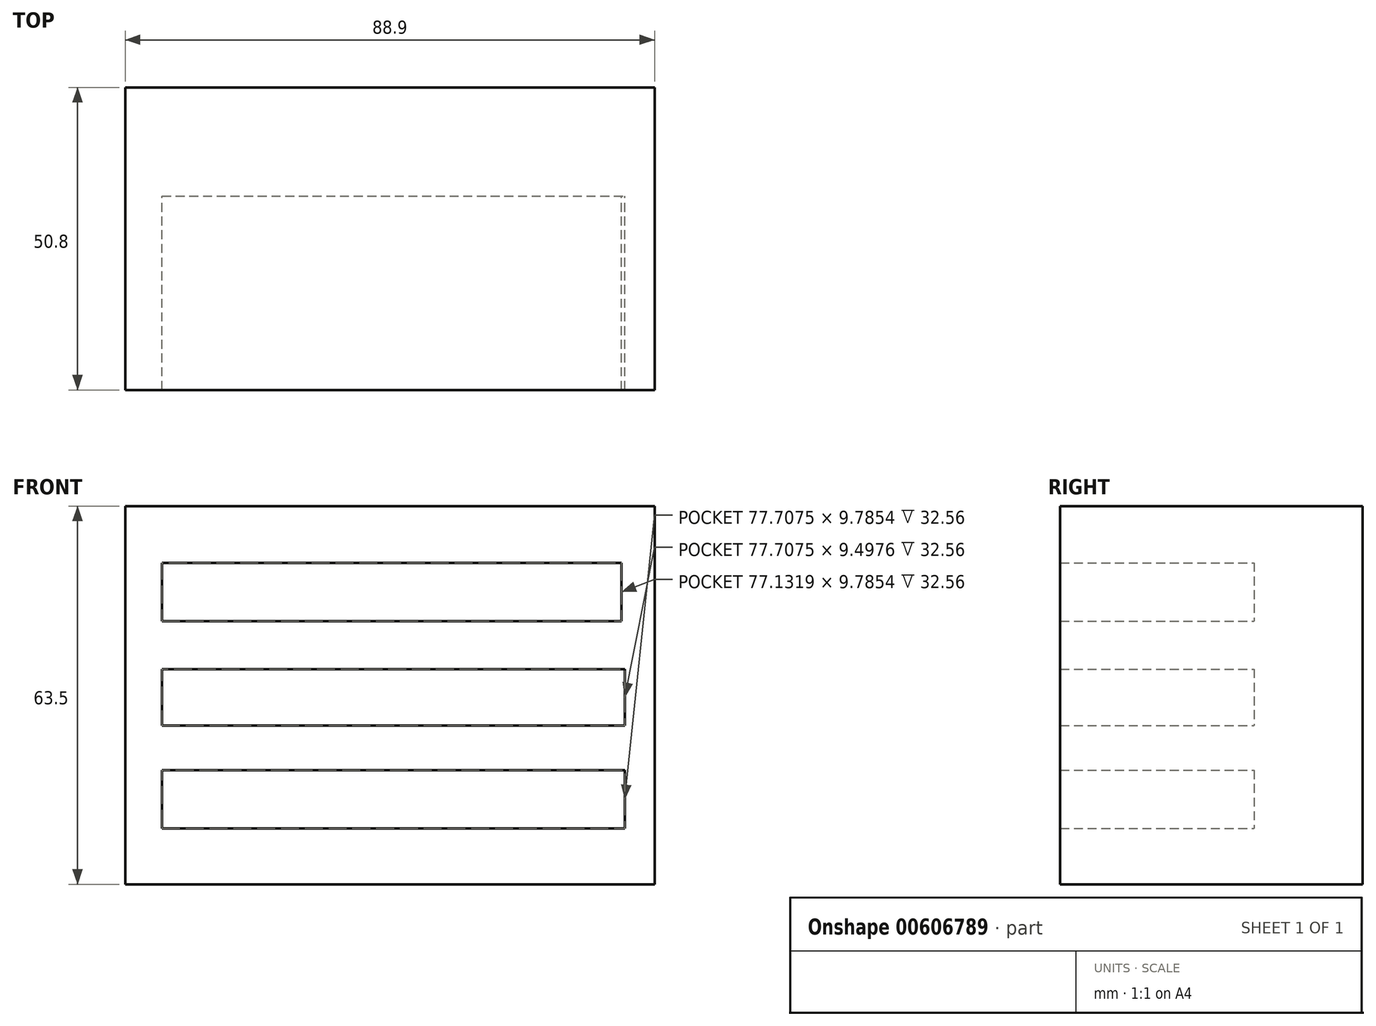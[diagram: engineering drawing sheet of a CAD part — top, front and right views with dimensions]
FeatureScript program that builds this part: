
annotation { "Feature Type Name" : "Feature", "Feature Type Description" : "" }
export const myFeature = defineFeature(function(context is Context, id is Id, definition is map)
    precondition{}
    {
        {
            var Q0;
            Q0=qCreatedBy(makeId("Top.planeOp"),FACE);
            var sketch = newSketch(context, id + "F0", { "sketchPlane" : qUnion([Q0])});
            skLineSegment(sketch, "E0.bottom", {"start": v(-37.69, 18.24) * mm, "end": v(51.21, 18.24) * mm});
            skLineSegment(sketch, "E0.top", {"start": v(-37.69, -32.56) * mm, "end": v(51.21, -32.56) * mm});
            skLineSegment(sketch, "E0.left", {"start": v(-37.69, 18.24) * mm, "end": v(-37.69, -32.56) * mm});
            skLineSegment(sketch, "E0.right", {"start": v(51.21, 18.24) * mm, "end": v(51.21, -32.56) * mm});
            skSolve(sketch);
        }
        {
            var Q0;
            Q0 = qSketchRegion(id + "F0", true);
            extrude(context, id + "F1", {"entities" : qUnion([Q0]), "depth" : 63.5 * mm, "offsetDistance" : 25.4 * mm});
        }
        {
            var Q0;
            Q0=qCreatedBy(makeId("Front.planeOp"),FACE);
            var sketch = newSketch(context, id + "F2", { "sketchPlane" : qUnion([Q0])});
            skLineSegment(sketch, "E1.bottom", {"start": v(-31.51, 53.96) * mm, "end": v(45.62, 53.96) * mm});
            skLineSegment(sketch, "E1.top", {"start": v(-31.51, 44.18) * mm, "end": v(45.62, 44.18) * mm});
            skLineSegment(sketch, "E1.left", {"start": v(-31.51, 53.96) * mm, "end": v(-31.51, 44.18) * mm});
            skLineSegment(sketch, "E1.right", {"start": v(45.62, 53.96) * mm, "end": v(45.62, 44.18) * mm});
            skLineSegment(sketch, "E2.bottom", {"start": v(-31.51, 36.12) * mm, "end": v(46.2, 36.12) * mm});
            skLineSegment(sketch, "E2.top", {"start": v(-31.51, 26.62) * mm, "end": v(46.2, 26.62) * mm});
            skLineSegment(sketch, "E2.left", {"start": v(-31.51, 36.12) * mm, "end": v(-31.51, 26.62) * mm});
            skLineSegment(sketch, "E2.right", {"start": v(46.2, 36.12) * mm, "end": v(46.2, 26.62) * mm});
            skLineSegment(sketch, "E3.bottom", {"start": v(-31.51, 19.14) * mm, "end": v(46.2, 19.14) * mm});
            skLineSegment(sketch, "E3.top", {"start": v(-31.51, 9.35) * mm, "end": v(46.2, 9.35) * mm});
            skLineSegment(sketch, "E3.left", {"start": v(-31.51, 19.14) * mm, "end": v(-31.51, 9.35) * mm});
            skLineSegment(sketch, "E3.right", {"start": v(46.2, 19.14) * mm, "end": v(46.2, 9.35) * mm});
            skSolve(sketch);
        }
        {
            var Q0;
            Q0 = qSketchRegion(id + "F2", true);
            extrude(context, id + "F3", {"entities" : qUnion([Q0]), "operationType" : NewBodyOperationType.REMOVE, "depth" : 127 * mm, "offsetDistance" : 25.4 * mm});
        }
    });
